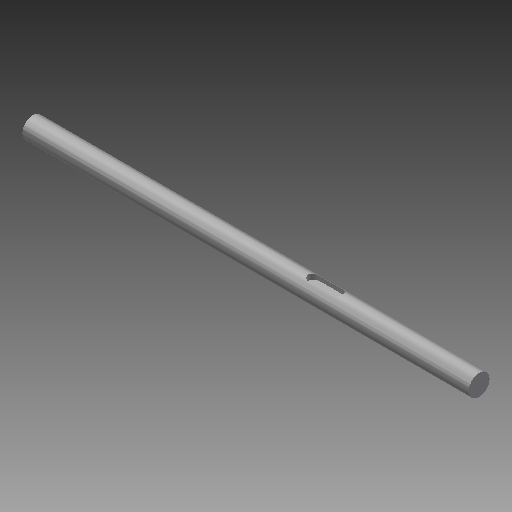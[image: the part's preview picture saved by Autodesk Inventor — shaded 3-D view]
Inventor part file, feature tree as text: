
AUTODESK INVENTOR PART (.ipt)
format: ipt  version: 2019 (Build 230136000, 136)  size: 320,512 bytes
history: native  units: in
note: dims shown in document units (in); Inventor stores cm internally (conversion verified against a paired STEP export)
features: other x7, revolve x1
ambient origin geometry x6: Origin, XZ Plane, XY Plane, X Axis, Y Axis, Z Axis
bodies: Solid1 (feature_tree)
feature tree (8):
  revolve  "Revolution1"  [1 undecoded]
  other  "Keyway1"
  other  "Keyway3"
  other  "Start Plane"
  other  "Origin point"
  other  "Main Sketch"
  other  "Shaft Keyway"
  other  "Shaft Keyway2"
note: 1 required parameter value undecoded (feature->parameter linkage not recoverable at this tier; creation-order binding heuristic only, values carry confidence <= 0.55)
